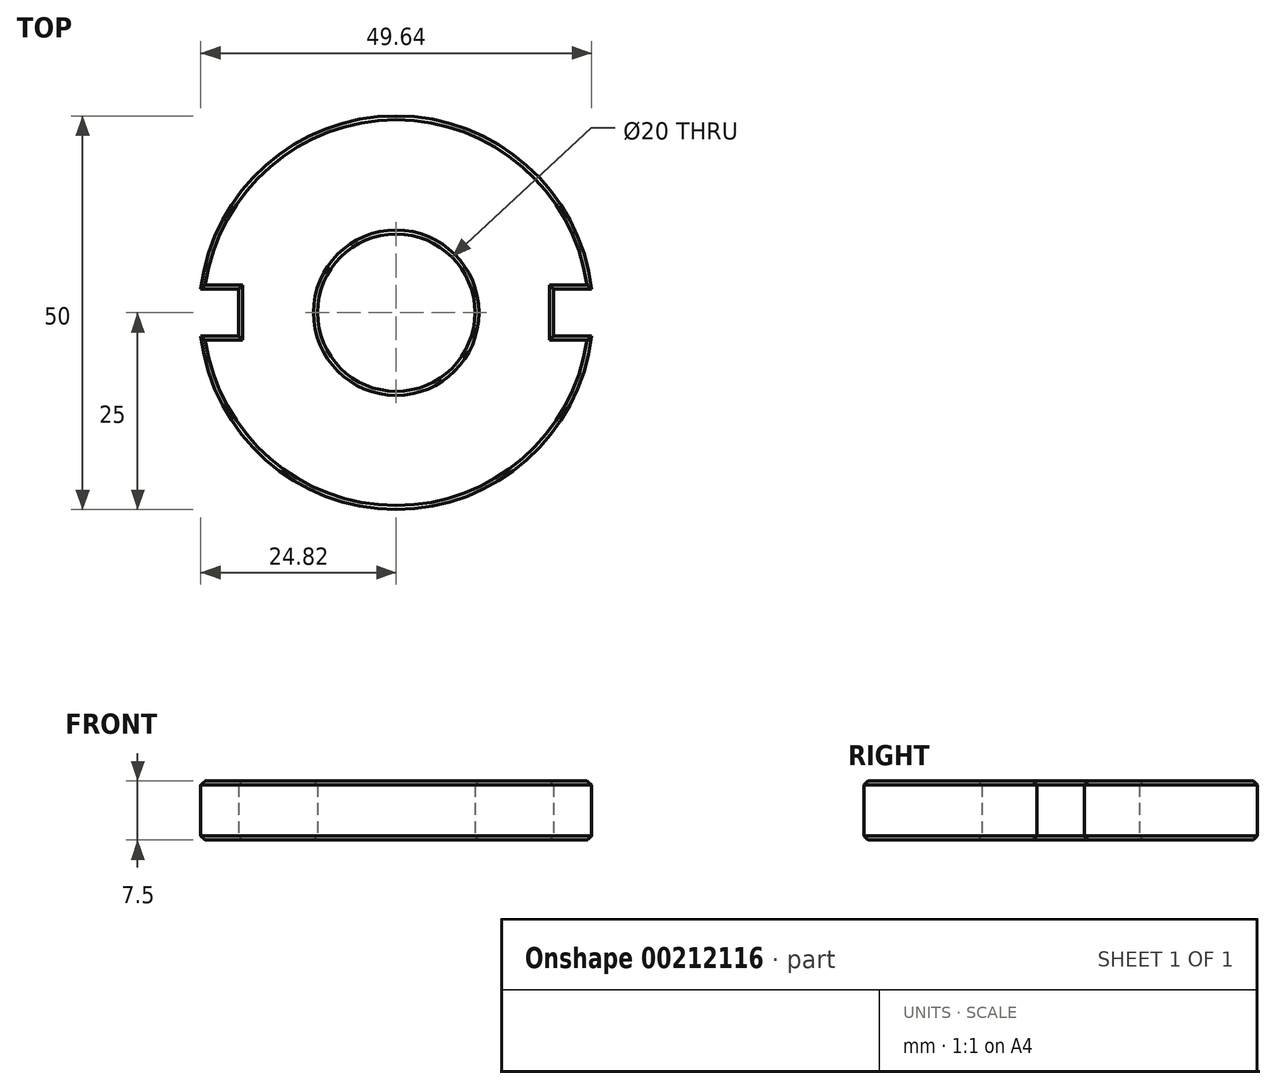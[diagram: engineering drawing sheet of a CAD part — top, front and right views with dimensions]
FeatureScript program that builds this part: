
annotation { "Feature Type Name" : "Feature", "Feature Type Description" : "" }
export const myFeature = defineFeature(function(context is Context, id is Id, definition is map)
    precondition{}
    {
        {
            var Q0;
            Q0=qCreatedBy(makeId("Top.planeOp"),FACE);
            var sketch = newSketch(context, id + "F0", { "sketchPlane" : qUnion([Q0])});
            skCircle(sketch, "E0", {"center": v(0, 0) * mm, "radius": 10 * mm});
            skCircle(sketch, "E1", {"center": v(0, 0) * mm, "radius": 25 * mm});
            skLineSegment(sketch, "E2", {"start": v(0, 0) * mm, "end": v(0, 25) * mm, "construction": true});
            skLineSegment(sketch, "E3", {"start": v(0, 0) * mm, "end": v(0, -25) * mm, "construction": true});
            skLineSegment(sketch, "E4", {"start": v(0, 0) * mm, "end": v(25, 0) * mm, "construction": true});
            skLineSegment(sketch, "E5", {"start": v(0, 0) * mm, "end": v(-25, 0) * mm, "construction": true});
            skLineSegment(sketch, "E6.bottom", {"start": v(-30, 3) * mm, "end": v(-20, 3) * mm});
            skLineSegment(sketch, "E6.top", {"start": v(-30, -3) * mm, "end": v(-20, -3) * mm});
            skLineSegment(sketch, "E6.left", {"start": v(-30, 3) * mm, "end": v(-30, -3) * mm});
            skLineSegment(sketch, "E6.right", {"start": v(-20, 3) * mm, "end": v(-20, -3) * mm});
            skPoint(sketch, "E6.middle", {"position": v(-25, 0) * mm});
            skLineSegment(sketch, "E7.1.0", {"start": v(30, 3) * mm, "end": v(20, 3) * mm});
            skLineSegment(sketch, "E7.1.1", {"start": v(30, -3) * mm, "end": v(30, 3) * mm});
            skLineSegment(sketch, "E7.1.2", {"start": v(30, -3) * mm, "end": v(20, -3) * mm});
            skLineSegment(sketch, "E7.1.3", {"start": v(20, -3) * mm, "end": v(20, 3) * mm});
            skSolve(sketch);
        }
        {
            var Q0;
            Q0=makeQuery(id+"F0.imprint","IMPRINT",FACE,{"disambiguationData":[TD([[makeQuery(id+"F0.imprint","IMPRINT",EDGE,{"derivedFrom":sQuery(id+"F0.wireOp",EDGE,"E0")}),-1.0]])]});
            extrude(context, id + "F1", {"entities" : qUnion([Q0]), "depth" : 7.5 * mm});
        }
        {
            var Q0;
            Q0=makeQuery(id+"F1.opExtrude","CAP_FACE",FACE,{"disambiguationData":[OSD([sQuery(id+"F0.wireOp",EDGE,"E0"),sQuery(id+"F0.wireOp",EDGE,"E1"),sQuery(id+"F0.wireOp",EDGE,"E6.bottom"),sQuery(id+"F0.wireOp",EDGE,"E6.top"),sQuery(id+"F0.wireOp",EDGE,"E6.right"),sQuery(id+"F0.wireOp",EDGE,"E7.1.0"),sQuery(id+"F0.wireOp",EDGE,"E7.1.2"),sQuery(id+"F0.wireOp",EDGE,"E7.1.3")])],"isStart":false});
            var Q1;
            Q1=makeQuery(id+"F1.opExtrude","CAP_FACE",FACE,{"disambiguationData":[OSD([sQuery(id+"F0.wireOp",EDGE,"E0"),sQuery(id+"F0.wireOp",EDGE,"E1"),sQuery(id+"F0.wireOp",EDGE,"E6.bottom"),sQuery(id+"F0.wireOp",EDGE,"E6.top"),sQuery(id+"F0.wireOp",EDGE,"E6.right"),sQuery(id+"F0.wireOp",EDGE,"E7.1.0"),sQuery(id+"F0.wireOp",EDGE,"E7.1.2"),sQuery(id+"F0.wireOp",EDGE,"E7.1.3")])],"isStart":true});
            chamfer(context, id + "F2", {"entities" : qUnion([Q0, Q1]), "width" : .5 * mm, "tangentPropagation" : true});
        }
    });
